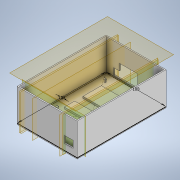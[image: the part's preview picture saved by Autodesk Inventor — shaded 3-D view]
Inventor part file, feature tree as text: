
AUTODESK INVENTOR PART (.ipt)
format: ipt  version: 2021 (Build 250183000, 183)  size: 396,800 bytes
history: native  units: in
note: dims shown in document units (in); Inventor stores cm internally (conversion verified against a paired STEP export)
features: sketch x22, extrude x16, reference x16, plane x7, other x4, revolve x2, mirror x2, chamfer x1
ambient origin geometry x8: Origin, YZ Plane, XZ Plane, XY Plane, X Axis, Y Axis, Z Axis, Center Point
bodies: Solid1 (feature_tree)
feature tree (70):
  sketch  "Sketch1"  dims[d0=3.937in d1=5.9055in]
  extrude  "Extrusion1"  Depth=5.9055in
  extrude  "Extrusion2"  Depth=2.1654in TaperAngle=0.0deg
  sketch  "Sketch2"  dims[d5=0.0787in d6=0.0in d7=-1.5748in]
  plane  "Work Plane1"
  extrude  "Extrusion3"  [1 undecoded]
  sketch  "Sketch7"  dims[d19=0.1181in d20=0.0in d21=2.8346in]
  plane  "Work Plane2"
  revolve  "Revolution2"  [1 undecoded]
  plane  "Work Plane3"
  extrude  "Extrusion4"  Depth=0.7087in
  sketch  "Sketch Driven Pattern1"  dims[d2=0.0787in d3=2.1654in d4=0.0in]
  extrude  "Extrusion5"  Depth=0.1181in
  plane  "Work Plane4"
  extrude  "Extrusion6"  Depth=0.1102in
  extrude  "Extrusion7"  Depth=0.1457in
  extrude  "Extrusion8"  TaperAngle=90.0deg  [1 undecoded]
  mirror  "Mirror1"
  plane  "Work Plane5"
  extrude  "Extrusion9"  Depth=0.0118in
  extrude  "Extrusion10"  Depth=0.0299in
  extrude  "Extrusion11"  Depth=0.0157in
  chamfer  "Chamfer1"  Distance=0.0787in
  extrude  "Extrusion12"  Depth=1.1811in
  sketch  "Sketch22"  dims[d47=0.5933in d48=0.0in d49=0.0866in]
  plane  "Work Plane6"
  revolve  "Revolution3"  [1 undecoded]
  extrude  "Extrusion13"  Depth=0.3819in
  sketch  "Sketch Driven Pattern2"  dims[d15=1.378in d16=1.2598in]
  extrude  "Extrusion14"  Depth=0.0866in
  extrude  "Extrusion15"  Depth=0.3236in
  extrude  "Extrusion16"  Depth=0.4724in
  plane  "Work Plane7"
  mirror  "Mirror2"
  sketch  "Sketch6"  dims[d17=1.0236in d18=0.7087in]
  reference  "Reference1"
  reference  "Reference2"
  reference  "Reference3"
  reference  "Reference4"
  sketch  "Sketch8"  dims[d22=0.7087in d23=0.1102in]
  sketch  "Sketch9"  dims[d26=0.1142in d27=0.1457in]
  sketch  "Sketch10"  dims[d28=0.1654in d30=90.0deg]
  reference  "Reference5"
  reference  "Reference6"
  reference  "Reference7"
  reference  "Reference8"
  reference  "Reference9"
  reference  "Reference10"
  sketch  "Sketch11"  dims[d31=3.0in d32=0.0118in]
  sketch  "Sketch13"  dims[d33=0.1946in d34=0.0299in]
  sketch  "Sketch15"  dims[d35=0.0787in d36=0.0in d37=0.0157in]
  sketch  "Sketch18"  dims[d38=0.0157in d39=0.0787in d40=0.0in]
  sketch  "Sketch19"  dims[d41=0.9055in d42=1.1811in]
  sketch  "Sketch20"  dims[d43=0.4606in d44=0.9843in]
  sketch  "Sketch21"  dims[d45=0.0906in d46=0.3819in]
  reference  "Reference11"
  reference  "Reference12"
  reference  "Reference13"
  reference  "Reference14"
  reference  "Reference15"
  reference  "Reference16"
  sketch  "Sketch25"  dims[d50=0.4409in d51=0.3236in]
  sketch  "Sketch26"  dims[d52=0.5933in d53=0.0in d54=0.4724in]
  sketch  "Sketch27"  dims[d55=0.5933in d56=0.0in]
  sketch  "Sketch29"  dims[d57=0.1575in d58=0.0787in d59=45.0deg]
  sketch  "Sketch30"  dims[d63=0.3937in d64=0.0906in d65=0.4606in d66=0.9843in d67=0.5933in d68=0.0in d69=0.0866in d70=0.4409in d71=0.3236in d72=0.5933in d73=0.0in d74=0.4724in d75=0.5933in d76=0.0in d77=0.2756in d78=0.5906in d79=0.1181in d80=0.0in d81=90.0deg d82=0.0276in d83=0.0394in d84=0.0in d85=0.2362in d86=0.5906in d87=0.3937in d88=0.2697in d89=0.0in d90=0.1496in d91=0.0591in d92=0.0in d93=0.0906in d94=0.1969in d95=0.0in d96=0.689in d97=0.0728in]
  other  "Chestbox_with_electronical_devices.iam"
  other  "ArduinoMega_STEP_AP203:1"
  other  "TCA9548A Adfruit with Header:1"
  other  "Part57"
note: 4 required parameter values undecoded (feature->parameter linkage not recoverable at this tier; creation-order binding heuristic only, values carry confidence <= 0.55)